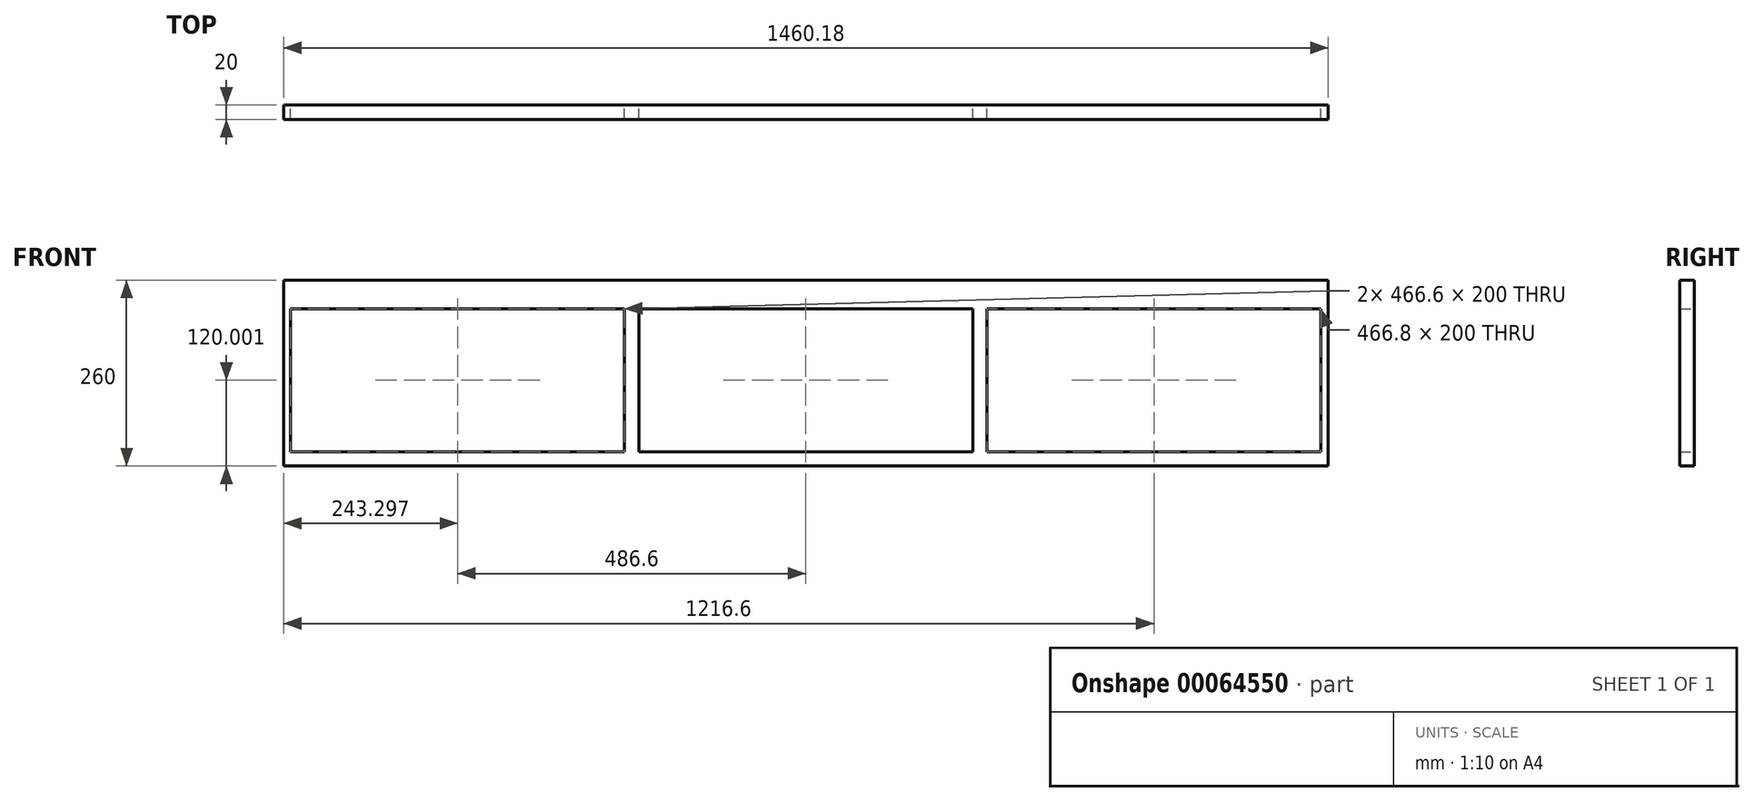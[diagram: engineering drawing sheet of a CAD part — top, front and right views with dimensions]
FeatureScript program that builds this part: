
annotation { "Feature Type Name" : "Feature", "Feature Type Description" : "" }
export const myFeature = defineFeature(function(context is Context, id is Id, definition is map)
    precondition{}
    {
        {
            var Q0;
            Q0=qCreatedBy(makeId("Front.planeOp"),FACE);
            var sketch = newSketch(context, id + "F0", { "sketchPlane" : qUnion([Q0])});
            skLineSegment(sketch, "E0", {"start": v(-734.61, 96.85) * mm, "end": v(725.39, 96.85) * mm});
            skLineSegment(sketch, "E1", {"start": v(725.39, 96.85) * mm, "end": v(725.39, 56.85) * mm});
            skLineSegment(sketch, "E2", {"start": v(715.39, 56.85) * mm, "end": v(248.59, 56.85) * mm});
            skLineSegment(sketch, "E3", {"start": v(248.59, 56.85) * mm, "end": v(248.59, -143.15) * mm});
            skLineSegment(sketch, "E4", {"start": v(248.59, -143.15) * mm, "end": v(228.59, -143.15) * mm});
            skLineSegment(sketch, "E5", {"start": v(228.59, -143.15) * mm, "end": v(228.59, 56.85) * mm});
            skLineSegment(sketch, "E6", {"start": v(228.59, 56.85) * mm, "end": v(-238.01, 56.85) * mm});
            skLineSegment(sketch, "E7", {"start": v(-238.01, 56.85) * mm, "end": v(-238.01, -143.15) * mm});
            skLineSegment(sketch, "E8", {"start": v(-238.01, -143.15) * mm, "end": v(-258.01, -143.15) * mm});
            skLineSegment(sketch, "E9", {"start": v(-258.01, -143.15) * mm, "end": v(-258.01, 56.85) * mm});
            skLineSegment(sketch, "E10", {"start": v(-258.01, 56.85) * mm, "end": v(-724.61, 56.85) * mm});
            skLineSegment(sketch, "E11", {"start": v(-734.61, 56.85) * mm, "end": v(-734.61, 96.85) * mm});
            skLineSegment(sketch, "E12", {"start": v(-724.61, 56.85) * mm, "end": v(-724.61, -143.15) * mm});
            skLineSegment(sketch, "E13", {"start": v(-734.61, 56.85) * mm, "end": v(-734.61, -143.15) * mm});
            skLineSegment(sketch, "E14", {"start": v(-724.61, -143.15) * mm, "end": v(-734.61, -143.15) * mm});
            skLineSegment(sketch, "E15", {"start": v(725.39, 56.85) * mm, "end": v(725.39, -143.15) * mm});
            skLineSegment(sketch, "E16", {"start": v(715.39, 56.85) * mm, "end": v(715.39, -143.15) * mm});
            skLineSegment(sketch, "E17", {"start": v(715.39, -143.15) * mm, "end": v(725.39, -143.15) * mm});
            skLineSegment(sketch, "E18", {"start": v(-724.61, -143.15) * mm, "end": v(-258.01, -143.15) * mm});
            skLineSegment(sketch, "E19", {"start": v(-238.01, -143.15) * mm, "end": v(228.59, -143.15) * mm});
            skLineSegment(sketch, "E20", {"start": v(248.59, -143.15) * mm, "end": v(715.39, -143.15) * mm});
            skLineSegment(sketch, "E21", {"start": v(-734.61, -143.15) * mm, "end": v(-734.61, -163.15) * mm});
            skLineSegment(sketch, "E22", {"start": v(-734.61, -163.15) * mm, "end": v(725.57, -163.15) * mm});
            skLineSegment(sketch, "E23", {"start": v(725.57, -163.15) * mm, "end": v(725.39, -143.15) * mm});
            skSolve(sketch);
        }
        {
            var Q0;
            Q0=makeQuery(id+"F0.imprint","IMPRINT",FACE,{"disambiguationData":[TD([[makeQuery(id+"F0.imprint","IMPRINT",EDGE,{"derivedFrom":sQuery(id+"F0.wireOp",EDGE,"E0")}),-1.0]])]});
            var Q1;
            Q1=makeQuery(id+"F0.imprint","IMPRINT",FACE,{"disambiguationData":[TD([[makeQuery(id+"F0.imprint","IMPRINT",EDGE,{"derivedFrom":sQuery(id+"F0.wireOp",EDGE,"E4")}),1.0]])]});
            extrude(context, id + "F1", {"entities" : qUnion([Q0, Q1]), "depth" : 20 * mm});
        }
    });
